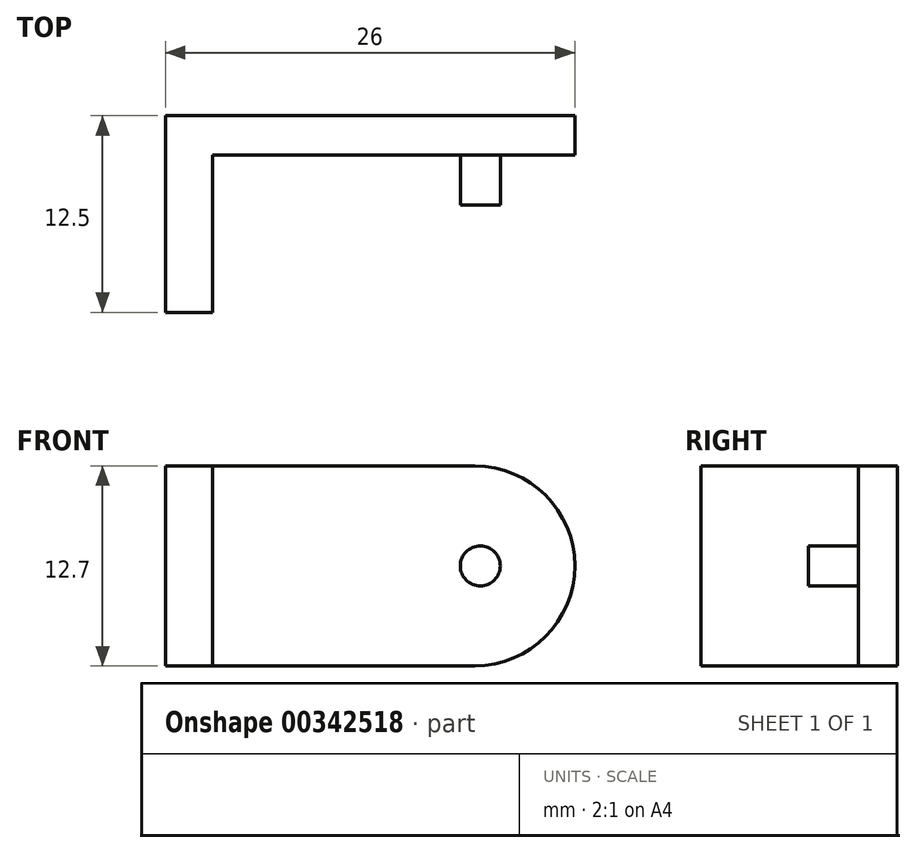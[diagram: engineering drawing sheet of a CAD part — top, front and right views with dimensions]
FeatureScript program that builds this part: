
annotation { "Feature Type Name" : "Feature", "Feature Type Description" : "" }
export const myFeature = defineFeature(function(context is Context, id is Id, definition is map)
    precondition{}
    {
        {
            var Q0;
            Q0=qCreatedBy(makeId("Top.planeOp"),FACE);
            var sketch = newSketch(context, id + "F0", { "sketchPlane" : qUnion([Q0])});
            skLineSegment(sketch, "E0", {"start": v(3, -12.5) * mm, "end": v(3, -2.5) * mm});
            skLineSegment(sketch, "E1", {"start": v(3, -2.5) * mm, "end": v(26, -2.5) * mm});
            skLineSegment(sketch, "E2", {"start": v(26, -2.5) * mm, "end": v(26, 0) * mm});
            skLineSegment(sketch, "E3", {"start": v(26, 0) * mm, "end": v(0, 0) * mm});
            skLineSegment(sketch, "E4", {"start": v(0, 0) * mm, "end": v(0, -12.5) * mm});
            skLineSegment(sketch, "E5", {"start": v(0, -12.5) * mm, "end": v(3, -12.5) * mm});
            skSolve(sketch);
        }
        {
            var Q0;
            Q0=makeQuery(id+"F0.imprint","IMPRINT",FACE,{"disambiguationData":[TD([[makeQuery(id+"F0.imprint","IMPRINT",EDGE,{"derivedFrom":sQuery(id+"F0.wireOp",EDGE,"E0")}),1.0]])]});
            extrude(context, id + "F1", {"entities" : qUnion([Q0]), "depth" : 12.7 * mm, "offsetDistance" : 25.4 * mm});
        }
        {
            var Q0;
            Q0=makeQuery(id+"F1.opExtrude","SWEPT_FACE",FACE,{"disambiguationData":[OSD([sQuery(id+"F0.wireOp",EDGE,"E1")])]});
            var sketch = newSketch(context, id + "F2", { "sketchPlane" : qUnion([Q0])});
            skPoint(sketch, "E6", {"position": v(20, 6.35) * mm});
            skCircle(sketch, "E7", {"center": v(20, 6.35) * mm, "radius": 1.27 * mm});
            skSolve(sketch);
        }
        {
            var Q0;
            Q0=makeQuery(id+"F2.imprint","IMPRINT",FACE,{"disambiguationData":[TD([[makeQuery(id+"F2.imprint","IMPRINT",EDGE,{"derivedFrom":sQuery(id+"F2.wireOp",EDGE,"E7")}),1.0]])]});
            extrude(context, id + "F3", {"entities" : qUnion([Q0]), "operationType" : NewBodyOperationType.ADD, "depth" : 3.17 * mm, "offsetDistance" : 25.4 * mm});
        }
        {
            var Q0;
            Q0=makeQuery(id+"F1.opExtrude","CAP_EDGE",EDGE,{"disambiguationData":[OSD([sQuery(id+"F0.wireOp",EDGE,"E2")])],"isStart":false});
            var Q1;
            Q1=makeQuery(id+"F1.opExtrude","CAP_EDGE",EDGE,{"disambiguationData":[OSD([sQuery(id+"F0.wireOp",EDGE,"E2")])],"isStart":true});
            fillet(context, id + "F4", {"entities" : qUnion([Q0, Q1]), "radius" : 6.35 * mm, "tangentPropagation" : true, "allowEdgeOverflow" : false});
        }
    });
